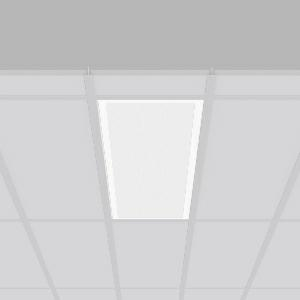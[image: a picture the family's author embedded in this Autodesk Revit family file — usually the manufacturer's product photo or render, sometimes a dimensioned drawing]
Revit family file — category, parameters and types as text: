
# Revit family: sidelite_eco_312368_002_1_790_5b45
name_source: partatom
category: Lighting Fixtures
units: mm (PartAtom-declared; Revit-internal decimal feet)

## family parameters
Cut with Voids When Loaded = No
Host = Face
Light Source = No
Part Type = Normal
Room Calculation Point = No
Round Connector Dimension = Use Diameter
Shared = No

## types (1)
- MultiLumen 1 (1 x LED Modul 840, 3500 lm, 4000)
    Apparent Load = 29 VA
    CIE Flux Codes = 64 88 97 100 100
    Color Rendering = 80
    Color Temperature = 4000
    Default Elevation = 1800 mm
    Description = Series: SIDELITE ECO
Highly economical recessed luminaire with progressive LED technology. Frame made of aluminium, powder-coated. Diffuser plastic microprismatic. Lightguide and diffuser made of non-yellowing plastic (PMMA). Lateral light emission (RZB SIDELITE technology) for homogeneous light distribution. External driver. External driver with simple plug-in locking system and extended converter connecting cable to luminaire (1.90 m). MultiLumen: 4 steps adjustable luminous flux. Factory setting is the lowest offered step. Luminaire can be used with accessories (to be ordered separately) as recessed or surface mounting luminaire. Perfect for office areas (RUG < 19) and environments with computer screens in accordance with EN 12464-1. Qualified for use in the food and drink industry. 
Colour: white
Length: 1245 mm
Width: 308 mm
Cut-out length: 1233 mm
Cut-out width: 296 mm
Recess height: 160 mm
Luminaire: recess height: 37 mm
Lamp: LED
Socket: without socket
Colour temperature: 4000K
Colour rendering index (CRI): 80
System power: 29 W
Rated luminous flux: 3500 lm
Luminous efficiency: 121 lm/W
System power 2: 33 W
Rated luminous flux 2: 3850 lm
Luminous efficiency 2: 117 lm/W
System power 3: 35 W
Rated luminous flux 3: 4050 lm
Luminous efficiency 3: 116 lm/W
System power 4: 38 W
Rated luminous flux 4: 4400 lm
Luminous efficiency 4: 116 lm/W
Control gear: Regulated power supply
Protection class: II
Type of protection: IP 40
    Height = 0 mm  [stored 0 ft]
    Lamp = 1 x LED Modul 840
    Lamp Light Flux = 3500 lm
    Lamp count = 1
    Length = 1245 mm
    Lifetime = 50000 h
    Luminous efficacy = 121 lm/W
    Manufacturer = RZB
    ModVariant = No
    Model = 312368.002.1.790
    Mounting Place = Ceiling
    Mounting Type = Recessed
    Number of Poles = 1
    OnlyDefault = Yes
    Power Factor = 1
    Product Name = SIDELITE ECO
    Product group = Recessed modular luminaires
    ProductGroupID = 406
    Protection Class = Protection class II
    Protection Degree = IP 20
    RLX_Detail_Level = 1
    RLX_Emergency_Light_Flux = 0 lm
    RLX_Emergency_Type = 0
    RLX_Emergency_Type_DB = No
    RlxData = <blob elided: 36073 chars, md5=273ff14a>
    Socket = socket
    Standby Power = 0 W
    System Light Flux = 3500 lm
    System Power = 29 W
    Type Comments = MultiLumen 1
    Type Image = 312368.002.jpg
    URL = http://relux.com
    VarID = multilumen_1
    Voltage = 230 V
    Voltage Range = 220-240 V
    Weight = 0.00 kg
    Width = 308 mm

note: [stored X ft] marks values corroborated as IEEE doubles in the binary element streams (Revit-internal decimal feet)

## geometry (parser evidence)
native form markers: Blend x4, Sweep x10
no freeform markers — native parametric forms only
